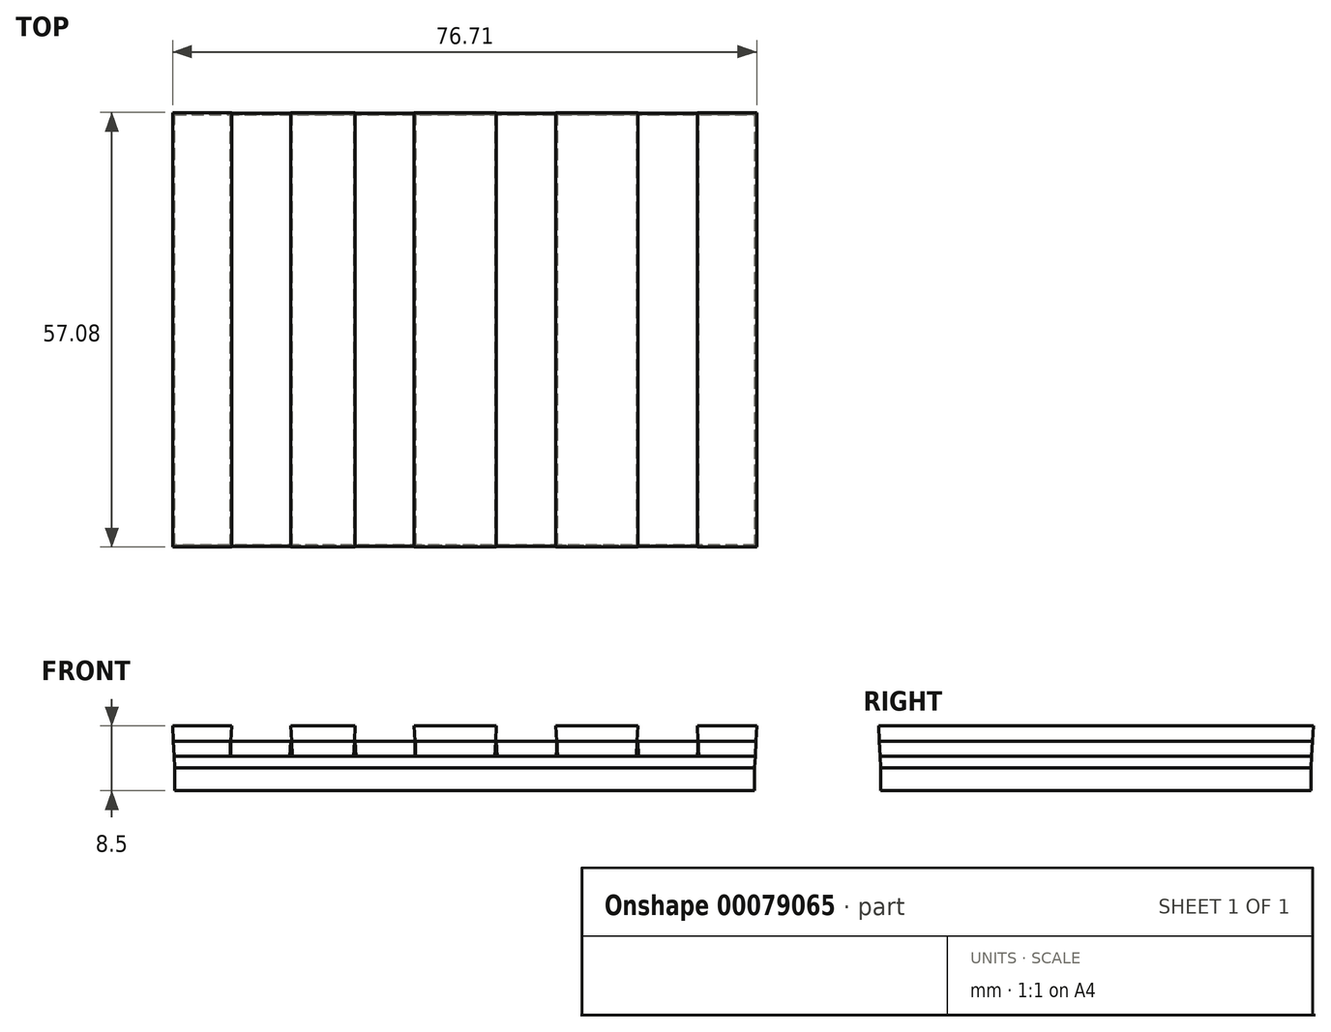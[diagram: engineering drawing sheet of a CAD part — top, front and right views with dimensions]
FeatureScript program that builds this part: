
annotation { "Feature Type Name" : "Feature", "Feature Type Description" : "" }
export const myFeature = defineFeature(function(context is Context, id is Id, definition is map)
    precondition{}
    {
        {
            var Q0;
            Q0=qCreatedBy(makeId("Top.planeOp"),FACE);
            var sketch = newSketch(context, id + "F0", { "sketchPlane" : qUnion([Q0])});
            skLineSegment(sketch, "E0.bottom", {"start": v(-76.14, 56.5) * mm, "end": v(0, 56.5) * mm});
            skLineSegment(sketch, "E0.top", {"start": v(-76.14, 0) * mm, "end": v(0, 0) * mm});
            skLineSegment(sketch, "E0.left", {"start": v(-76.14, 56.5) * mm, "end": v(-76.14, 0) * mm});
            skLineSegment(sketch, "E0.right", {"start": v(0, 56.5) * mm, "end": v(0, 0) * mm});
            skSolve(sketch);
        }
        {
            var Q0;
            Q0=qSketchRegion(id+"F0",true);
            extrude(context, id + "F1", {"entities" : qUnion([Q0]), "depth" : 3 * mm});
        }
        {
            var Q0;
            Q0=makeQuery(id+"F1.opExtrude","CAP_FACE",FACE,{"disambiguationData":[OSD([sQuery(id+"F0.wireOp",EDGE,"E0.bottom"),sQuery(id+"F0.wireOp",EDGE,"E0.top"),sQuery(id+"F0.wireOp",EDGE,"E0.left"),sQuery(id+"F0.wireOp",EDGE,"E0.right")])],"isStart":false});
            var sketch = newSketch(context, id + "F2", { "sketchPlane" : qUnion([Q0])});
            skLineSegment(sketch, "E1.bottom", {"start": v(-76.14, 56.5) * mm, "end": v(0, 56.5) * mm});
            skLineSegment(sketch, "E1.top", {"start": v(-76.14, 0) * mm, "end": v(0, 0) * mm});
            skLineSegment(sketch, "E1.left", {"start": v(-76.14, 56.5) * mm, "end": v(-76.14, 0) * mm});
            skLineSegment(sketch, "E1.right", {"start": v(0, 56.5) * mm, "end": v(0, 0) * mm});
            skSolve(sketch);
        }
        {
            var Q0;
            Q0=makeQuery(id+"F2.imprint","IMPRINT",FACE,{"disambiguationData":[TD([[makeQuery(id+"F2.imprint","IMPRINT",EDGE,{"derivedFrom":sQuery(id+"F2.wireOp",EDGE,"E1.bottom")}),-1.0]])]});
            extrude(context, id + "F3", {"entities" : qUnion([Q0]), "depth" : 1.5 * mm, "hasDraft" : true, "draftAngle" : 3 * degree});
        }
        {
            var Q0;
            Q0=makeQuery(id+"F3.opExtrude","CAP_FACE",FACE,{"disambiguationData":[OSD([sQuery(id+"F2.wireOp",EDGE,"E1.bottom"),sQuery(id+"F2.wireOp",EDGE,"E1.top"),sQuery(id+"F2.wireOp",EDGE,"E1.left"),sQuery(id+"F2.wireOp",EDGE,"E1.right")])],"isStart":false});
            var sketch = newSketch(context, id + "F4", { "sketchPlane" : qUnion([Q0])});
            skLineSegment(sketch, "E2.bottom", {"start": v(-76.22, 56.58) * mm, "end": v(0.08, 56.58) * mm});
            skLineSegment(sketch, "E2.top", {"start": v(-76.22, -0.08) * mm, "end": v(0.08, -0.08) * mm});
            skLineSegment(sketch, "E2.left", {"start": v(-76.22, 56.58) * mm, "end": v(-76.22, -0.08) * mm});
            skLineSegment(sketch, "E2.right", {"start": v(0.08, 56.58) * mm, "end": v(0.08, -0.08) * mm});
            skSolve(sketch);
        }
        {
            var Q0;
            Q0=qSketchRegion(id+"F4",true);
            extrude(context, id + "F5", {"entities" : qUnion([Q0]), "depth" : 2 * mm, "hasDraft" : true, "draftAngle" : 3 * degree});
        }
        {
            var Q0;
            Q0=makeQuery(id+"F5.opExtrude","CAP_FACE",FACE,{"disambiguationData":[OSD([sQuery(id+"F4.wireOp",EDGE,"E2.bottom"),sQuery(id+"F4.wireOp",EDGE,"E2.top"),sQuery(id+"F4.wireOp",EDGE,"E2.left"),sQuery(id+"F4.wireOp",EDGE,"E2.right")])],"isStart":false});
            var sketch = newSketch(context, id + "F6", { "sketchPlane" : qUnion([Q0])});
            skLineSegment(sketch, "E3.bottom", {"start": v(-68.76, 56.68) * mm, "end": v(-60.82, 56.68) * mm});
            skLineSegment(sketch, "E3.top", {"start": v(-68.76, -0.18) * mm, "end": v(-60.82, -0.18) * mm});
            skLineSegment(sketch, "E3.left", {"start": v(-68.76, 56.68) * mm, "end": v(-68.76, -0.18) * mm});
            skLineSegment(sketch, "E3.right", {"start": v(-60.82, 56.68) * mm, "end": v(-60.82, -0.18) * mm});
            skSolve(sketch);
        }
        {
            var Q0;
            Q0=qSketchRegion(id+"F6",true);
            extrude(context, id + "F7", {"entities" : qUnion([Q0]), "operationType" : NewBodyOperationType.REMOVE, "oppositeDirection" : true, "depth" : 2 * mm, "hasDraft" : true, "draftAngle" : 3 * degree});
        }
        {
            var Q0;
            {var subQ0=sQuery(id+"F4.wireOp",EDGE,"E2.bottom");var subQ1=sQuery(id+"F4.wireOp",EDGE,"E2.top");var subQ2=sQuery(id+"F4.wireOp",EDGE,"E2.right");Q0=makeQuery(id+"F7.boolean.opBoolean","SPLIT",FACE,{"disambiguationData":[TD([makeQuery(id+"F5.opExtrude","SWEPT_FACE",FACE,{"disambiguationData":[OSD([subQ2])]})])],"derivedFrom":makeQuery(id+"F5.opExtrude","CAP_FACE",FACE,{"disambiguationData":[OSD([subQ0,subQ1,sQuery(id+"F4.wireOp",EDGE,"E2.left"),subQ2])],"isStart":false})});}
            var sketch = newSketch(context, id + "F8", { "sketchPlane" : qUnion([Q0])});
            skLineSegment(sketch, "E4.bottom", {"start": v(-52.56, 56.68) * mm, "end": v(-44.62, 56.68) * mm});
            skLineSegment(sketch, "E4.top", {"start": v(-52.56, -0.18) * mm, "end": v(-44.62, -0.18) * mm});
            skLineSegment(sketch, "E4.left", {"start": v(-52.56, 56.68) * mm, "end": v(-52.56, -0.18) * mm});
            skLineSegment(sketch, "E4.right", {"start": v(-44.62, 56.68) * mm, "end": v(-44.62, -0.18) * mm});
            skSolve(sketch);
        }
        {
            var Q0;
            Q0=qSketchRegion(id+"F8",true);
            extrude(context, id + "F9", {"entities" : qUnion([Q0]), "operationType" : NewBodyOperationType.REMOVE, "oppositeDirection" : true, "depth" : 2 * mm, "hasDraft" : true, "draftAngle" : 3 * degree});
        }
        {
            var Q0;
            {var subQ0=sQuery(id+"F4.wireOp",EDGE,"E2.bottom");var subQ2=sQuery(id+"F4.wireOp",EDGE,"E2.top");var subQ4=sQuery(id+"F4.wireOp",EDGE,"E2.right");var subQ5=makeQuery(id+"F5.opExtrude","SWEPT_FACE",FACE,{"disambiguationData":[OSD([subQ4])]});Q0=makeQuery(id+"F9.boolean.opBoolean","SPLIT",FACE,{"disambiguationData":[TD([subQ5])],"derivedFrom":makeQuery(id+"F7.boolean.opBoolean","SPLIT",FACE,{"disambiguationData":[TD([subQ5])],"derivedFrom":makeQuery(id+"F5.opExtrude","CAP_FACE",FACE,{"disambiguationData":[OSD([subQ0,subQ2,sQuery(id+"F4.wireOp",EDGE,"E2.left"),subQ4])],"isStart":false})})});}
            var sketch = newSketch(context, id + "F10", { "sketchPlane" : qUnion([Q0])});
            skLineSegment(sketch, "E5.bottom", {"start": v(-34, 56.68) * mm, "end": v(-25.99, 56.68) * mm});
            skLineSegment(sketch, "E5.top", {"start": v(-34, -0.18) * mm, "end": v(-25.99, -0.18) * mm});
            skLineSegment(sketch, "E5.left", {"start": v(-34, 56.68) * mm, "end": v(-34, -0.18) * mm});
            skLineSegment(sketch, "E5.right", {"start": v(-25.99, 56.68) * mm, "end": v(-25.99, -0.18) * mm});
            skSolve(sketch);
        }
        {
            var Q0;
            Q0=qSketchRegion(id+"F10",true);
            extrude(context, id + "F11", {"entities" : qUnion([Q0]), "operationType" : NewBodyOperationType.REMOVE, "oppositeDirection" : true, "depth" : 2 * mm, "hasDraft" : true, "draftAngle" : 3 * degree});
        }
        {
            var Q0;
            {var subQ0=sQuery(id+"F4.wireOp",EDGE,"E2.bottom");var subQ2=sQuery(id+"F4.wireOp",EDGE,"E2.top");var subQ4=sQuery(id+"F4.wireOp",EDGE,"E2.right");var subQ5=makeQuery(id+"F5.opExtrude","SWEPT_FACE",FACE,{"disambiguationData":[OSD([subQ4])]});Q0=makeQuery(id+"F11.boolean.opBoolean","SPLIT",FACE,{"disambiguationData":[TD([subQ5])],"derivedFrom":makeQuery(id+"F9.boolean.opBoolean","SPLIT",FACE,{"disambiguationData":[TD([subQ5])],"derivedFrom":makeQuery(id+"F7.boolean.opBoolean","SPLIT",FACE,{"disambiguationData":[TD([subQ5])],"derivedFrom":makeQuery(id+"F5.opExtrude","CAP_FACE",FACE,{"disambiguationData":[OSD([subQ0,subQ2,sQuery(id+"F4.wireOp",EDGE,"E2.left"),subQ4])],"isStart":false})})})});}
            var sketch = newSketch(context, id + "F12", { "sketchPlane" : qUnion([Q0])});
            skLineSegment(sketch, "E6.bottom", {"start": v(-15.44, 56.68) * mm, "end": v(-7.42, 56.68) * mm});
            skLineSegment(sketch, "E6.top", {"start": v(-15.44, -0.18) * mm, "end": v(-7.42, -0.18) * mm});
            skLineSegment(sketch, "E6.left", {"start": v(-15.44, 56.68) * mm, "end": v(-15.44, -0.18) * mm});
            skLineSegment(sketch, "E6.right", {"start": v(-7.42, 56.68) * mm, "end": v(-7.42, -0.18) * mm});
            skSolve(sketch);
        }
        {
            var Q0;
            Q0=qSketchRegion(id+"F12",true);
            extrude(context, id + "F13", {"entities" : qUnion([Q0]), "operationType" : NewBodyOperationType.REMOVE, "oppositeDirection" : true, "depth" : 2 * mm, "hasDraft" : true, "draftAngle" : 3 * degree});
        }
        {
            var Q0;
            {var subQ0=sQuery(id+"F4.wireOp",EDGE,"E2.bottom");var subQ1=sQuery(id+"F4.wireOp",EDGE,"E2.top");var subQ2=sQuery(id+"F4.wireOp",EDGE,"E2.left");Q0=makeQuery(id+"F7.boolean.opBoolean","SPLIT",FACE,{"disambiguationData":[TD([makeQuery(id+"F5.opExtrude","SWEPT_FACE",FACE,{"disambiguationData":[OSD([subQ2])]})])],"derivedFrom":makeQuery(id+"F5.opExtrude","CAP_FACE",FACE,{"disambiguationData":[OSD([subQ0,subQ1,subQ2,sQuery(id+"F4.wireOp",EDGE,"E2.right")])],"isStart":false})});}
            var sketch = newSketch(context, id + "F14", { "sketchPlane" : qUnion([Q0])});
            skLineSegment(sketch, "E7.bottom", {"start": v(-76.32, 56.68) * mm, "end": v(-68.76, 56.68) * mm});
            skLineSegment(sketch, "E7.top", {"start": v(-76.32, -0.18) * mm, "end": v(-68.76, -0.18) * mm});
            skLineSegment(sketch, "E7.left", {"start": v(-76.32, 56.68) * mm, "end": v(-76.32, -0.18) * mm});
            skLineSegment(sketch, "E7.right", {"start": v(-68.76, 56.68) * mm, "end": v(-68.76, -0.18) * mm});
            skSolve(sketch);
        }
        {
            var Q0;
            Q0=qSketchRegion(id+"F14",true);
            extrude(context, id + "F15", {"entities" : qUnion([Q0]), "depth" : 2 * mm, "hasDraft" : true, "draftAngle" : 3 * degree});
        }
        {
            var Q0;
            {var subQ0=sQuery(id+"F4.wireOp",EDGE,"E2.bottom");var subQ2=sQuery(id+"F4.wireOp",EDGE,"E2.top");var subQ4=makeQuery(id+"F7.opExtrude","SWEPT_FACE",FACE,{"disambiguationData":[OSD([sQuery(id+"F6.wireOp",EDGE,"E3.right")])]});var subQ5=sQuery(id+"F4.wireOp",EDGE,"E2.right");Q0=makeQuery(id+"F9.boolean.opBoolean","SPLIT",FACE,{"disambiguationData":[TD([makeQuery(id+"F7.boolean.opBoolean","COPY",FACE,{"derivedFrom":subQ4})])],"derivedFrom":makeQuery(id+"F7.boolean.opBoolean","SPLIT",FACE,{"disambiguationData":[TD([makeQuery(id+"F5.opExtrude","SWEPT_FACE",FACE,{"disambiguationData":[OSD([subQ5])]})])],"derivedFrom":makeQuery(id+"F5.opExtrude","CAP_FACE",FACE,{"disambiguationData":[OSD([subQ0,subQ2,sQuery(id+"F4.wireOp",EDGE,"E2.left"),subQ5])],"isStart":false})})});}
            var sketch = newSketch(context, id + "F16", { "sketchPlane" : qUnion([Q0])});
            skLineSegment(sketch, "E8.bottom", {"start": v(-60.82, 56.68) * mm, "end": v(-52.56, 56.68) * mm});
            skLineSegment(sketch, "E8.top", {"start": v(-60.82, -0.18) * mm, "end": v(-52.56, -0.18) * mm});
            skLineSegment(sketch, "E8.left", {"start": v(-60.82, 56.68) * mm, "end": v(-60.82, -0.18) * mm});
            skLineSegment(sketch, "E8.right", {"start": v(-52.56, 56.68) * mm, "end": v(-52.56, -0.18) * mm});
            skSolve(sketch);
        }
        {
            var Q0;
            Q0=qSketchRegion(id+"F16",true);
            extrude(context, id + "F17", {"entities" : qUnion([Q0]), "depth" : 2 * mm, "hasDraft" : true, "draftAngle" : 3 * degree});
        }
        {
            var Q0;
            Q0=makeQuery(id+"F3.opExtrude","CAP_FACE",FACE,{"disambiguationData":[OSD([sQuery(id+"F2.wireOp",EDGE,"E1.bottom"),sQuery(id+"F2.wireOp",EDGE,"E1.top"),sQuery(id+"F2.wireOp",EDGE,"E1.left"),sQuery(id+"F2.wireOp",EDGE,"E1.right")])],"isStart":false});
            var sketch = newSketch(context, id + "F18", { "sketchPlane" : qUnion([Q0])});
            skLineSegment(sketch, "E9.bottom", {"start": v(-68.78, 56.58) * mm, "end": v(-61.04, 56.58) * mm});
            skLineSegment(sketch, "E9.top", {"start": v(-68.78, -0.08) * mm, "end": v(-61.04, -0.08) * mm});
            skLineSegment(sketch, "E9.left", {"start": v(-68.78, 56.58) * mm, "end": v(-68.78, -0.08) * mm});
            skLineSegment(sketch, "E9.right", {"start": v(-61.04, 56.58) * mm, "end": v(-61.04, -0.08) * mm});
            skSolve(sketch);
        }
        {
            var Q0;
            Q0=qSketchRegion(id+"F18",true);
            extrude(context, id + "F19", {"entities" : qUnion([Q0]), "depth" : 2 * mm, "hasDraft" : true, "draftAngle" : 3 * degree});
        }
        {
            var Q0;
            Q0=makeQuery(id+"F3.opExtrude","CAP_FACE",FACE,{"disambiguationData":[OSD([sQuery(id+"F2.wireOp",EDGE,"E1.bottom"),sQuery(id+"F2.wireOp",EDGE,"E1.top"),sQuery(id+"F2.wireOp",EDGE,"E1.left"),sQuery(id+"F2.wireOp",EDGE,"E1.right")])],"isStart":false});
            var sketch = newSketch(context, id + "F20", { "sketchPlane" : qUnion([Q0])});
            skLineSegment(sketch, "E10.bottom", {"start": v(-52.37, 56.58) * mm, "end": v(-44.62, 56.58) * mm});
            skLineSegment(sketch, "E10.top", {"start": v(-52.37, -0.08) * mm, "end": v(-44.62, -0.08) * mm});
            skLineSegment(sketch, "E10.left", {"start": v(-52.37, 56.58) * mm, "end": v(-52.37, -0.08) * mm});
            skLineSegment(sketch, "E10.right", {"start": v(-44.62, 56.58) * mm, "end": v(-44.62, -0.08) * mm});
            skSolve(sketch);
        }
        {
            var Q0;
            Q0=qSketchRegion(id+"F20",true);
            extrude(context, id + "F21", {"entities" : qUnion([Q0]), "depth" : 2 * mm, "hasDraft" : true, "draftAngle" : 3 * degree});
        }
        {
            var Q0;
            {var subQ0=sQuery(id+"F4.wireOp",EDGE,"E2.bottom");var subQ2=sQuery(id+"F4.wireOp",EDGE,"E2.top");var subQ4=makeQuery(id+"F9.opExtrude","SWEPT_FACE",FACE,{"disambiguationData":[OSD([sQuery(id+"F8.wireOp",EDGE,"E4.right")])]});var subQ5=sQuery(id+"F4.wireOp",EDGE,"E2.right");var subQ6=makeQuery(id+"F5.opExtrude","SWEPT_FACE",FACE,{"disambiguationData":[OSD([subQ5])]});Q0=makeQuery(id+"F11.boolean.opBoolean","SPLIT",FACE,{"disambiguationData":[TD([makeQuery(id+"F9.boolean.opBoolean","COPY",FACE,{"derivedFrom":subQ4})])],"derivedFrom":makeQuery(id+"F9.boolean.opBoolean","SPLIT",FACE,{"disambiguationData":[TD([subQ6])],"derivedFrom":makeQuery(id+"F7.boolean.opBoolean","SPLIT",FACE,{"disambiguationData":[TD([subQ6])],"derivedFrom":makeQuery(id+"F5.opExtrude","CAP_FACE",FACE,{"disambiguationData":[OSD([subQ0,subQ2,sQuery(id+"F4.wireOp",EDGE,"E2.left"),subQ5])],"isStart":false})})})});}
            var sketch = newSketch(context, id + "F22", { "sketchPlane" : qUnion([Q0])});
            skLineSegment(sketch, "E11.bottom", {"start": v(-44.62, 56.68) * mm, "end": v(-34, 56.68) * mm});
            skLineSegment(sketch, "E11.top", {"start": v(-44.62, -0.18) * mm, "end": v(-34, -0.18) * mm});
            skLineSegment(sketch, "E11.left", {"start": v(-44.62, 56.68) * mm, "end": v(-44.62, -0.18) * mm});
            skLineSegment(sketch, "E11.right", {"start": v(-34, 56.68) * mm, "end": v(-34, -0.18) * mm});
            skSolve(sketch);
        }
        {
            var Q0;
            Q0=qSketchRegion(id+"F22",true);
            extrude(context, id + "F23", {"entities" : qUnion([Q0]), "depth" : 2 * mm, "hasDraft" : true, "draftAngle" : 3 * degree});
        }
        {
            var Q0;
            Q0=makeQuery(id+"F3.opExtrude","CAP_FACE",FACE,{"disambiguationData":[OSD([sQuery(id+"F2.wireOp",EDGE,"E1.bottom"),sQuery(id+"F2.wireOp",EDGE,"E1.top"),sQuery(id+"F2.wireOp",EDGE,"E1.left"),sQuery(id+"F2.wireOp",EDGE,"E1.right")])],"isStart":false});
            var sketch = newSketch(context, id + "F24", { "sketchPlane" : qUnion([Q0])});
            skLineSegment(sketch, "E12.bottom", {"start": v(-33.8, 56.58) * mm, "end": v(-26.06, 56.58) * mm});
            skLineSegment(sketch, "E12.top", {"start": v(-33.8, -0.08) * mm, "end": v(-26.06, -0.08) * mm});
            skLineSegment(sketch, "E12.left", {"start": v(-33.8, 56.58) * mm, "end": v(-33.8, -0.08) * mm});
            skLineSegment(sketch, "E12.right", {"start": v(-26.06, 56.58) * mm, "end": v(-26.06, -0.08) * mm});
            skSolve(sketch);
        }
        {
            var Q0;
            Q0=qSketchRegion(id+"F24",true);
            extrude(context, id + "F25", {"entities" : qUnion([Q0]), "depth" : 2 * mm, "hasDraft" : true, "draftAngle" : 3 * degree});
        }
        {
            var Q0;
            {var subQ0=sQuery(id+"F4.wireOp",EDGE,"E2.bottom");var subQ2=sQuery(id+"F4.wireOp",EDGE,"E2.top");var subQ4=makeQuery(id+"F11.opExtrude","SWEPT_FACE",FACE,{"disambiguationData":[OSD([sQuery(id+"F10.wireOp",EDGE,"E5.right")])]});var subQ5=sQuery(id+"F4.wireOp",EDGE,"E2.right");var subQ6=makeQuery(id+"F5.opExtrude","SWEPT_FACE",FACE,{"disambiguationData":[OSD([subQ5])]});Q0=makeQuery(id+"F13.boolean.opBoolean","SPLIT",FACE,{"disambiguationData":[TD([makeQuery(id+"F11.boolean.opBoolean","COPY",FACE,{"derivedFrom":subQ4})])],"derivedFrom":makeQuery(id+"F11.boolean.opBoolean","SPLIT",FACE,{"disambiguationData":[TD([subQ6])],"derivedFrom":makeQuery(id+"F9.boolean.opBoolean","SPLIT",FACE,{"disambiguationData":[TD([subQ6])],"derivedFrom":makeQuery(id+"F7.boolean.opBoolean","SPLIT",FACE,{"disambiguationData":[TD([subQ6])],"derivedFrom":makeQuery(id+"F5.opExtrude","CAP_FACE",FACE,{"disambiguationData":[OSD([subQ0,subQ2,sQuery(id+"F4.wireOp",EDGE,"E2.left"),subQ5])],"isStart":false})})})})});}
            var sketch = newSketch(context, id + "F26", { "sketchPlane" : qUnion([Q0])});
            skLineSegment(sketch, "E13.bottom", {"start": v(-25.99, 56.68) * mm, "end": v(-15.44, 56.68) * mm});
            skLineSegment(sketch, "E13.top", {"start": v(-25.99, -0.18) * mm, "end": v(-15.44, -0.18) * mm});
            skLineSegment(sketch, "E13.left", {"start": v(-25.99, 56.68) * mm, "end": v(-25.99, -0.18) * mm});
            skLineSegment(sketch, "E13.right", {"start": v(-15.44, 56.68) * mm, "end": v(-15.44, -0.18) * mm});
            skSolve(sketch);
        }
        {
            var Q0;
            Q0=qSketchRegion(id+"F26",true);
            extrude(context, id + "F27", {"entities" : qUnion([Q0]), "depth" : 2 * mm, "hasDraft" : true, "draftAngle" : 3 * degree});
        }
        {
            var Q0;
            Q0=makeQuery(id+"F3.opExtrude","CAP_FACE",FACE,{"disambiguationData":[OSD([sQuery(id+"F2.wireOp",EDGE,"E1.bottom"),sQuery(id+"F2.wireOp",EDGE,"E1.top"),sQuery(id+"F2.wireOp",EDGE,"E1.left"),sQuery(id+"F2.wireOp",EDGE,"E1.right")])],"isStart":false});
            var sketch = newSketch(context, id + "F28", { "sketchPlane" : qUnion([Q0])});
            skLineSegment(sketch, "E14.bottom", {"start": v(-15.24, 56.58) * mm, "end": v(-7.49, 56.58) * mm});
            skLineSegment(sketch, "E14.top", {"start": v(-15.24, -0.08) * mm, "end": v(-7.49, -0.08) * mm});
            skLineSegment(sketch, "E14.left", {"start": v(-15.24, 56.58) * mm, "end": v(-15.24, -0.08) * mm});
            skLineSegment(sketch, "E14.right", {"start": v(-7.49, 56.58) * mm, "end": v(-7.49, -0.08) * mm});
            skSolve(sketch);
        }
        {
            var Q0;
            Q0=qSketchRegion(id+"F28",true);
            extrude(context, id + "F29", {"entities" : qUnion([Q0]), "depth" : 2 * mm, "hasDraft" : true, "draftAngle" : 3 * degree});
        }
        {
            var Q0;
            {var subQ0=sQuery(id+"F4.wireOp",EDGE,"E2.bottom");var subQ2=sQuery(id+"F4.wireOp",EDGE,"E2.top");var subQ4=sQuery(id+"F4.wireOp",EDGE,"E2.right");var subQ5=makeQuery(id+"F5.opExtrude","SWEPT_FACE",FACE,{"disambiguationData":[OSD([subQ4])]});Q0=makeQuery(id+"F13.boolean.opBoolean","SPLIT",FACE,{"disambiguationData":[TD([subQ5])],"derivedFrom":makeQuery(id+"F11.boolean.opBoolean","SPLIT",FACE,{"disambiguationData":[TD([subQ5])],"derivedFrom":makeQuery(id+"F9.boolean.opBoolean","SPLIT",FACE,{"disambiguationData":[TD([subQ5])],"derivedFrom":makeQuery(id+"F7.boolean.opBoolean","SPLIT",FACE,{"disambiguationData":[TD([subQ5])],"derivedFrom":makeQuery(id+"F5.opExtrude","CAP_FACE",FACE,{"disambiguationData":[OSD([subQ0,subQ2,sQuery(id+"F4.wireOp",EDGE,"E2.left"),subQ4])],"isStart":false})})})})});}
            var sketch = newSketch(context, id + "F30", { "sketchPlane" : qUnion([Q0])});
            skLineSegment(sketch, "E15.bottom", {"start": v(-7.42, 56.68) * mm, "end": v(0.18, 56.68) * mm});
            skLineSegment(sketch, "E15.top", {"start": v(-7.42, -0.18) * mm, "end": v(0.18, -0.18) * mm});
            skLineSegment(sketch, "E15.left", {"start": v(-7.42, 56.68) * mm, "end": v(-7.42, -0.18) * mm});
            skLineSegment(sketch, "E15.right", {"start": v(0.18, 56.68) * mm, "end": v(0.18, -0.18) * mm});
            skSolve(sketch);
        }
        {
            var Q0;
            Q0=qSketchRegion(id+"F30",true);
            extrude(context, id + "F31", {"entities" : qUnion([Q0]), "depth" : 2 * mm, "hasDraft" : true, "draftAngle" : 3 * degree});
        }
    });
